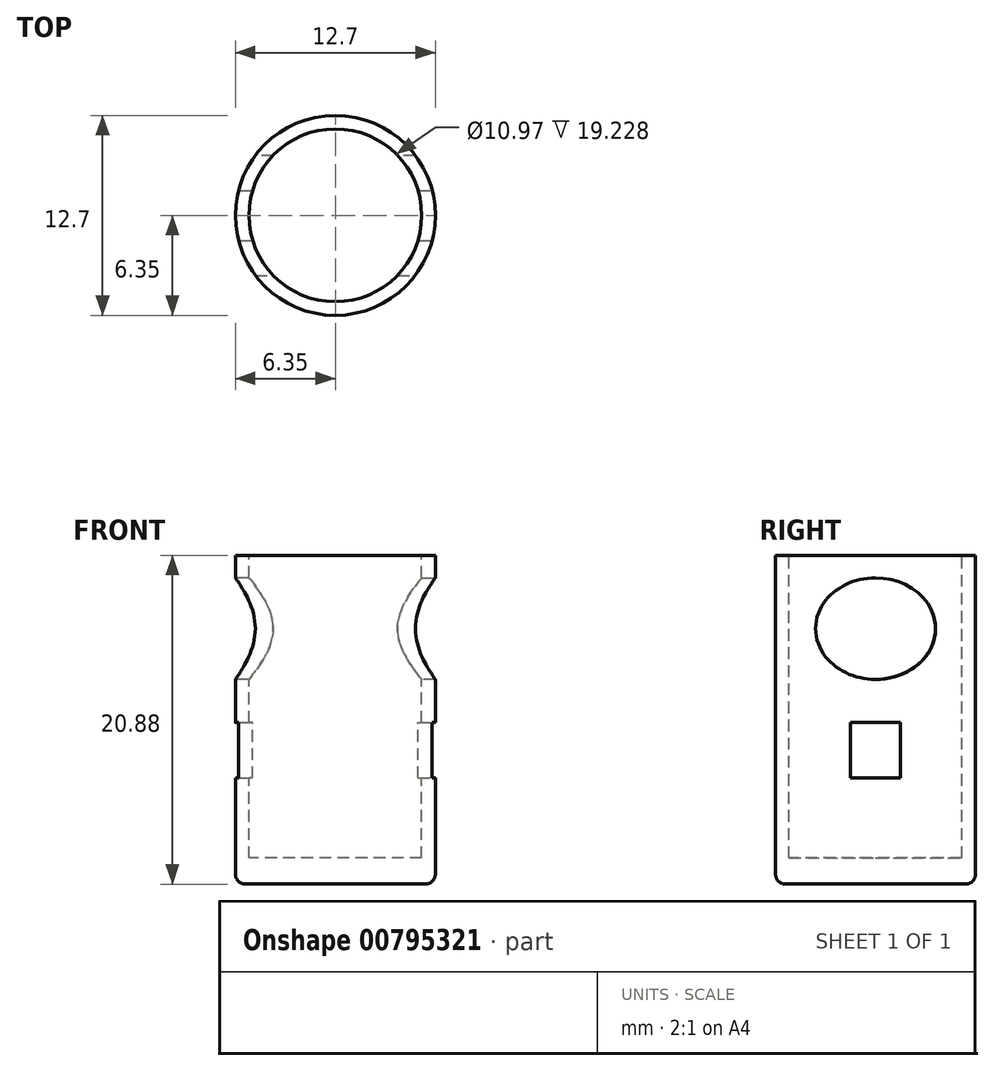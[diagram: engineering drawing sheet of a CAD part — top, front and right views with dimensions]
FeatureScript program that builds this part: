
annotation { "Feature Type Name" : "Feature", "Feature Type Description" : "" }
export const myFeature = defineFeature(function(context is Context, id is Id, definition is map)
    precondition{}
    {
        {
            var Q0;
            Q0=qCreatedBy(makeId("Top.planeOp"),FACE);
            var sketch = newSketch(context, id + "F0", { "sketchPlane" : qUnion([Q0])});
            skCircle(sketch, "E0", {"center": v(0, 0) * mm, "radius": 6.35 * mm});
            skSolve(sketch);
        }
        {
            var Q0;
            Q0 = qSketchRegion(id + "F0", true);
            extrude(context, id + "F1", {"entities" : qUnion([Q0]), "endBound" : BoundingType.SYMMETRIC, "depth" : 20.88 * mm, "offsetDistance" : 25.4 * mm});
        }
        {
            var Q0;
            Q0=makeQuery(id+"F1.opExtrude","CAP_FACE",FACE,{"disambiguationData":[OSD([sQuery(id+"F0.wireOp",EDGE,"E0")])],"isStart":false});
            var sketch = newSketch(context, id + "F2", { "sketchPlane" : qUnion([Q0])});
            skCircle(sketch, "E1", {"center": v(0, 0) * mm, "radius": 5.49 * mm});
            skSolve(sketch);
        }
        {
            var Q0;
            Q0 = qSketchRegion(id + "F2", true);
            extrude(context, id + "F3", {"entities" : qUnion([Q0]), "operationType" : NewBodyOperationType.REMOVE, "oppositeDirection" : true, "depth" : 19.23 * mm, "offsetDistance" : 25.4 * mm});
        }
        {
            var Q0;
            Q0=qCreatedBy(makeId("Right.planeOp"),FACE);
            var sketch = newSketch(context, id + "F4", { "sketchPlane" : qUnion([Q0])});
            skLineSegment(sketch, "E2.bottom", {"start": v(-1.59, -0.18) * mm, "end": v(1.59, -0.18) * mm});
            skLineSegment(sketch, "E2.top", {"start": v(-1.59, -3.7) * mm, "end": v(1.59, -3.7) * mm});
            skLineSegment(sketch, "E2.left", {"start": v(-1.59, -0.18) * mm, "end": v(-1.59, -3.7) * mm});
            skLineSegment(sketch, "E2.right", {"start": v(1.59, -0.18) * mm, "end": v(1.59, -3.7) * mm});
            skPoint(sketch, "E2.middle", {"position": v(0, -1.94) * mm});
            skSolve(sketch);
        }
        {
            var Q0;
            Q0 = qSketchRegion(id + "F4", true);
            extrude(context, id + "F5", {"entities" : qUnion([Q0]), "operationType" : NewBodyOperationType.REMOVE, "endBound" : BoundingType.SYMMETRIC, "oppositeDirection" : true, "depth" : 25.4 * mm, "offsetDistance" : 25.4 * mm});
        }
        {
            var Q0;
            Q0=qCreatedBy(makeId("Right.planeOp"),FACE);
            var sketch = newSketch(context, id + "F6", { "sketchPlane" : qUnion([Q0])});
            skEllipse(sketch, "E3", {"center": v(0, 5.8) * mm, "majorRadius": 3.23 * mm, "minorRadius": 3.81 * mm, "majorAxis": v(0, 1)});
            skSolve(sketch);
        }
        {
            var Q0;
            Q0 = qSketchRegion(id + "F6", true);
            extrude(context, id + "F7", {"entities" : qUnion([Q0]), "operationType" : NewBodyOperationType.REMOVE, "endBound" : BoundingType.SYMMETRIC, "oppositeDirection" : true, "depth" : 25.4 * mm, "offsetDistance" : 25.4 * mm});
        }
        {
            var Q0;
            Q0=makeQuery(id+"F1.opExtrude","CAP_EDGE",EDGE,{"disambiguationData":[OSD([sQuery(id+"F0.wireOp",EDGE,"E0")])],"isStart":true});
            fillet(context, id + "F8", {"entities" : qUnion([Q0]), "radius" : 0.64 * mm, "tangentPropagation" : true, "allowEdgeOverflow" : false});
        }
    });
